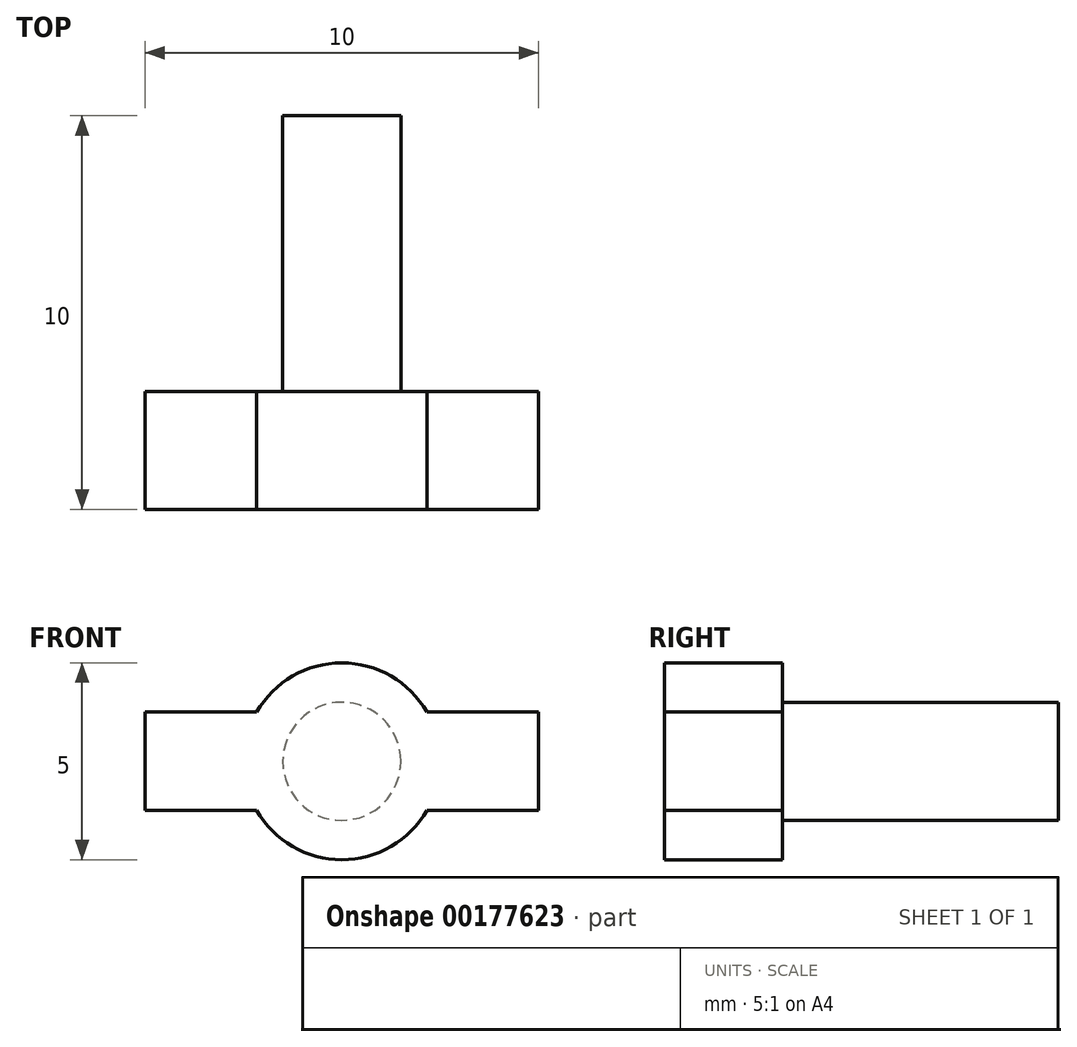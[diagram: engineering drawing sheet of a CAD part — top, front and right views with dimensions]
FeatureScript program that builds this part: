
annotation { "Feature Type Name" : "Feature", "Feature Type Description" : "" }
export const myFeature = defineFeature(function(context is Context, id is Id, definition is map)
    precondition{}
    {
        {
            var Q0;
            Q0=qCreatedBy(makeId("Front.planeOp"),FACE);
            var sketch = newSketch(context, id + "F0", { "sketchPlane" : qUnion([Q0])});
            skCircle(sketch, "E0", {"center": v(0, 0) * mm, "radius": 1.5 * mm});
            skSolve(sketch);
        }
        {
            var Q0;
            Q0=qSketchRegion(id+"F0",true);
            extrude(context, id + "F1", {"entities" : qUnion([Q0]), "depth" : 7 * mm});
        }
        {
            var Q0;
            Q0=makeQuery(id+"F1.opExtrude","CAP_FACE",FACE,{"disambiguationData":[OSD([sQuery(id+"F0.wireOp",EDGE,"E0")])],"isStart":false});
            var sketch = newSketch(context, id + "F2", { "sketchPlane" : qUnion([Q0])});
            skCircle(sketch, "E1", {"center": v(0, 0) * mm, "radius": 2.5 * mm});
            skLineSegment(sketch, "E2.bottom", {"start": v(5, 1.25) * mm, "end": v(-5, 1.25) * mm});
            skLineSegment(sketch, "E2.top", {"start": v(5, -1.25) * mm, "end": v(-5, -1.25) * mm});
            skLineSegment(sketch, "E2.left", {"start": v(5, 1.25) * mm, "end": v(5, -1.25) * mm});
            skLineSegment(sketch, "E2.right", {"start": v(-5, 1.25) * mm, "end": v(-5, -1.25) * mm});
            skSolve(sketch);
        }
        {
            var Q0;
            Q0=qSketchRegion(id+"F2",true);
            extrude(context, id + "F3", {"entities" : qUnion([Q0]), "operationType" : NewBodyOperationType.ADD, "depth" : 3 * mm});
        }
    });
